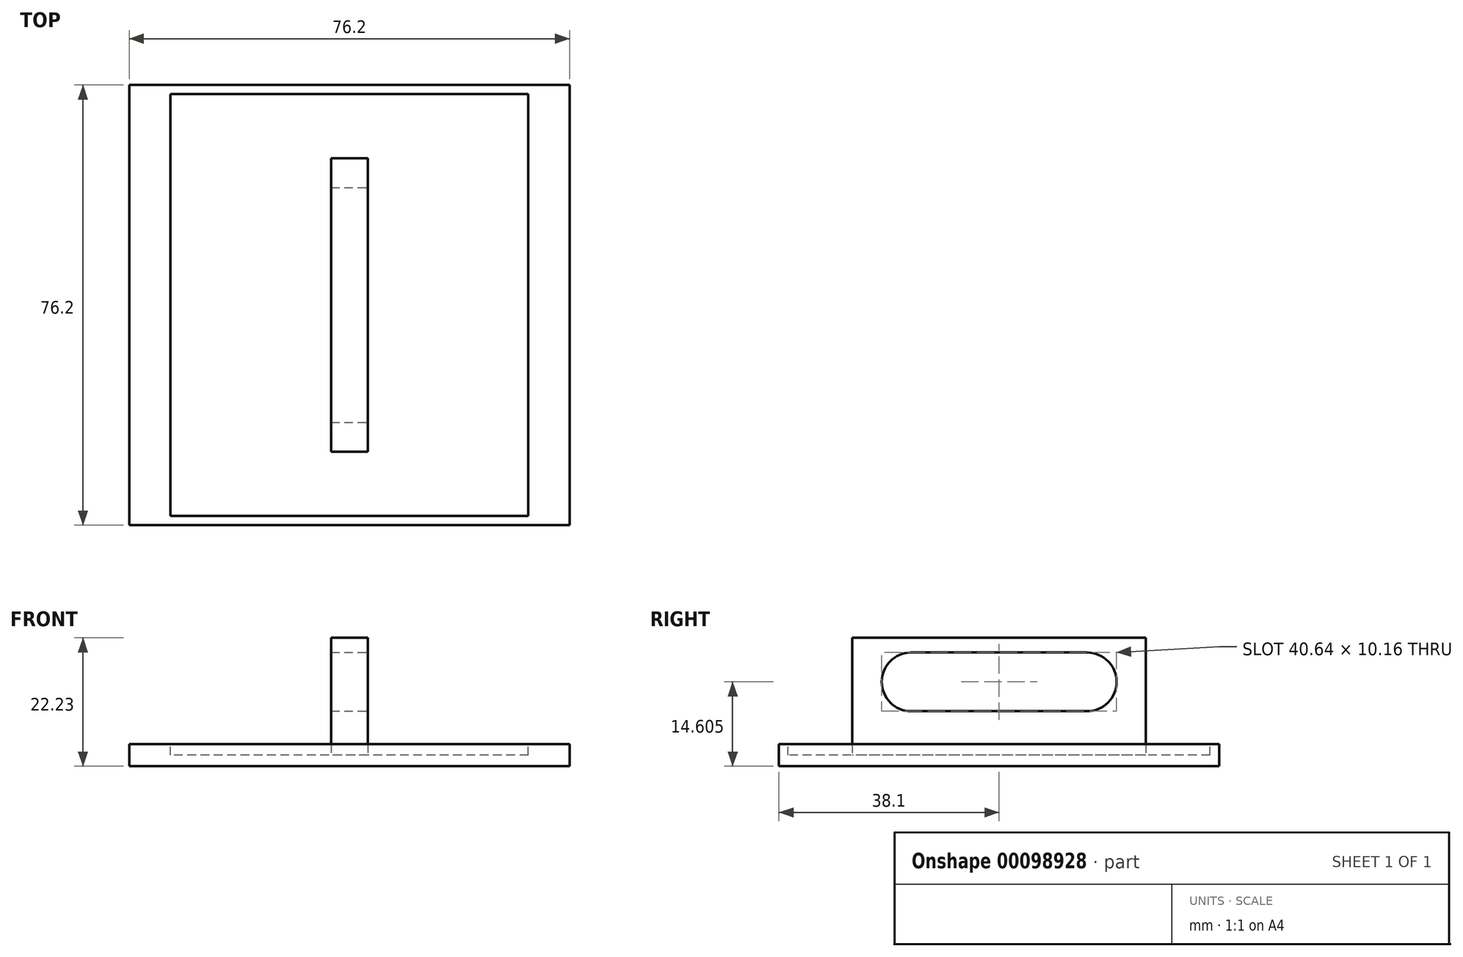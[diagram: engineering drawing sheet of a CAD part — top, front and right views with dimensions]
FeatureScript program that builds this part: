
annotation { "Feature Type Name" : "Feature", "Feature Type Description" : "" }
export const myFeature = defineFeature(function(context is Context, id is Id, definition is map)
    precondition{}
    {
        {
            var Q0;
            Q0=qCreatedBy(makeId("Top.planeOp"),FACE);
            var sketch = newSketch(context, id + "F0", { "sketchPlane" : qUnion([Q0])});
            skLineSegment(sketch, "E0.bottom", {"start": v(38.1, 38.1) * mm, "end": v(-38.1, 38.1) * mm});
            skLineSegment(sketch, "E0.top", {"start": v(38.1, -38.1) * mm, "end": v(-38.1, -38.1) * mm});
            skLineSegment(sketch, "E0.left", {"start": v(38.1, 38.1) * mm, "end": v(38.1, -38.1) * mm});
            skLineSegment(sketch, "E0.right", {"start": v(-38.1, 38.1) * mm, "end": v(-38.1, -38.1) * mm});
            skPoint(sketch, "E0.middle", {"position": v(0, 0) * mm});
            skSolve(sketch);
        }
        {
            var Q0;
            Q0=qSketchRegion(id+"F0",true);
            extrude(context, id + "F1", {"entities" : qUnion([Q0]), "depth" : 3.8 * mm});
        }
        {
            var Q0;
            Q0=makeQuery(id+"F1.opExtrude","CAP_FACE",FACE,{"disambiguationData":[OSD([sQuery(id+"F0.wireOp",EDGE,"E0.bottom"),sQuery(id+"F0.wireOp",EDGE,"E0.top"),sQuery(id+"F0.wireOp",EDGE,"E0.left"),sQuery(id+"F0.wireOp",EDGE,"E0.right")])],"isStart":false});
            var sketch = newSketch(context, id + "F2", { "sketchPlane" : qUnion([Q0])});
            skLineSegment(sketch, "E1.bottom", {"start": v(30.96, 36.51) * mm, "end": v(-30.96, 36.51) * mm});
            skLineSegment(sketch, "E1.top", {"start": v(30.96, -36.51) * mm, "end": v(-30.96, -36.51) * mm});
            skLineSegment(sketch, "E1.left", {"start": v(30.96, 36.51) * mm, "end": v(30.96, -36.51) * mm});
            skLineSegment(sketch, "E1.right", {"start": v(-30.96, 36.51) * mm, "end": v(-30.96, -36.51) * mm});
            skPoint(sketch, "E1.middle", {"position": v(0, 0) * mm});
            skSolve(sketch);
        }
        {
            var Q0;
            Q0=qSketchRegion(id+"F2",true);
            extrude(context, id + "F3", {"entities" : qUnion([Q0]), "operationType" : NewBodyOperationType.REMOVE, "oppositeDirection" : true, "depth" : 1.9 * mm});
        }
        {
            var Q0;
            Q0=makeQuery(id+"F3.boolean.opBoolean","COPY",FACE,{"derivedFrom":makeQuery(id+"F3.opExtrude","CAP_FACE",FACE,{"disambiguationData":[OSD([sQuery(id+"F2.wireOp",EDGE,"E1.bottom"),sQuery(id+"F2.wireOp",EDGE,"E1.top"),sQuery(id+"F2.wireOp",EDGE,"E1.left"),sQuery(id+"F2.wireOp",EDGE,"E1.right")])],"isStart":false})});
            var sketch = newSketch(context, id + "F4", { "sketchPlane" : qUnion([Q0])});
            skLineSegment(sketch, "E2.bottom", {"start": v(3.18, 25.4) * mm, "end": v(-3.17, 25.4) * mm});
            skLineSegment(sketch, "E2.top", {"start": v(3.17, -25.4) * mm, "end": v(-3.18, -25.4) * mm});
            skLineSegment(sketch, "E2.left", {"start": v(3.18, 25.4) * mm, "end": v(3.17, -25.4) * mm});
            skLineSegment(sketch, "E2.right", {"start": v(-3.17, 25.4) * mm, "end": v(-3.18, -25.4) * mm});
            skPoint(sketch, "E2.middle", {"position": v(0, 0) * mm});
            skSolve(sketch);
        }
        {
            var Q0;
            Q0=qSketchRegion(id+"F4",true);
            extrude(context, id + "F5", {"entities" : qUnion([Q0]), "operationType" : NewBodyOperationType.ADD, "depth" : 25.4 * mm});
        }
        {
            var Q0;
            Q0=makeQuery(id+"F5.opExtrude","SWEPT_FACE",FACE,{"disambiguationData":[OSD([sQuery(id+"F4.wireOp",EDGE,"E2.left")])]});
            var sketch = newSketch(context, id + "F6", { "sketchPlane" : qUnion([Q0])});
            skLineSegment(sketch, "E3.bottom", {"start": v(15.24, 19.69) * mm, "end": v(-15.24, 19.69) * mm});
            skLineSegment(sketch, "E3.top", {"start": v(15.24, 9.53) * mm, "end": v(-15.24, 9.53) * mm});
            skPoint(sketch, "E3.middle", {"position": v(0, 14.6) * mm});
            skPoint(sketch, "E3.middle.positionSnap0", {"position": v(-25.4, 14.6) * mm});
            skPoint(sketch, "E3.middle.positionSnap1", {"position": v(0, 27.3) * mm});
            skPoint(sketch, "E3.centerSnap0", {"position": v(-25.4, 14.6) * mm});
            skPoint(sketch, "E3.centerSnap1", {"position": v(0, 27.3) * mm});
            skArc(sketch, "E4", {"start": v(-15.24, 19.69) * mm, "mid": v(-20.32, 14.6) * mm, "end": v(-15.24, 9.53) * mm});
            skArc(sketch, "E5", {"start": v(15.24, 9.53) * mm, "mid": v(20.32, 14.6) * mm, "end": v(15.24, 19.69) * mm});
            skSolve(sketch);
        }
        {
            var Q0;
            Q0=qSketchRegion(id+"F6",true);
            extrude(context, id + "F7", {"entities" : qUnion([Q0]), "operationType" : NewBodyOperationType.REMOVE, "oppositeDirection" : true, "depth" : 25.4 * mm});
        }
        {
            var Q0;
            Q0=makeQuery(id+"F5.opExtrude","SWEPT_FACE",FACE,{"disambiguationData":[OSD([sQuery(id+"F4.wireOp",EDGE,"E2.left")])]});
            var sketch = newSketch(context, id + "F8", { "sketchPlane" : qUnion([Q0])});
            skLineSegment(sketch, "E6.bottom", {"start": v(-25.4, 27.3) * mm, "end": v(25.4, 27.3) * mm});
            skLineSegment(sketch, "E6.top", {"start": v(-25.4, 22.23) * mm, "end": v(25.4, 22.23) * mm});
            skLineSegment(sketch, "E6.left", {"start": v(-25.4, 27.3) * mm, "end": v(-25.4, 22.23) * mm});
            skLineSegment(sketch, "E6.right", {"start": v(25.4, 27.3) * mm, "end": v(25.4, 22.23) * mm});
            skSolve(sketch);
        }
        {
            var Q0;
            Q0=qSketchRegion(id+"F8",true);
            extrude(context, id + "F9", {"entities" : qUnion([Q0]), "operationType" : NewBodyOperationType.REMOVE, "oppositeDirection" : true, "depth" : 25.4 * mm});
        }
    });
